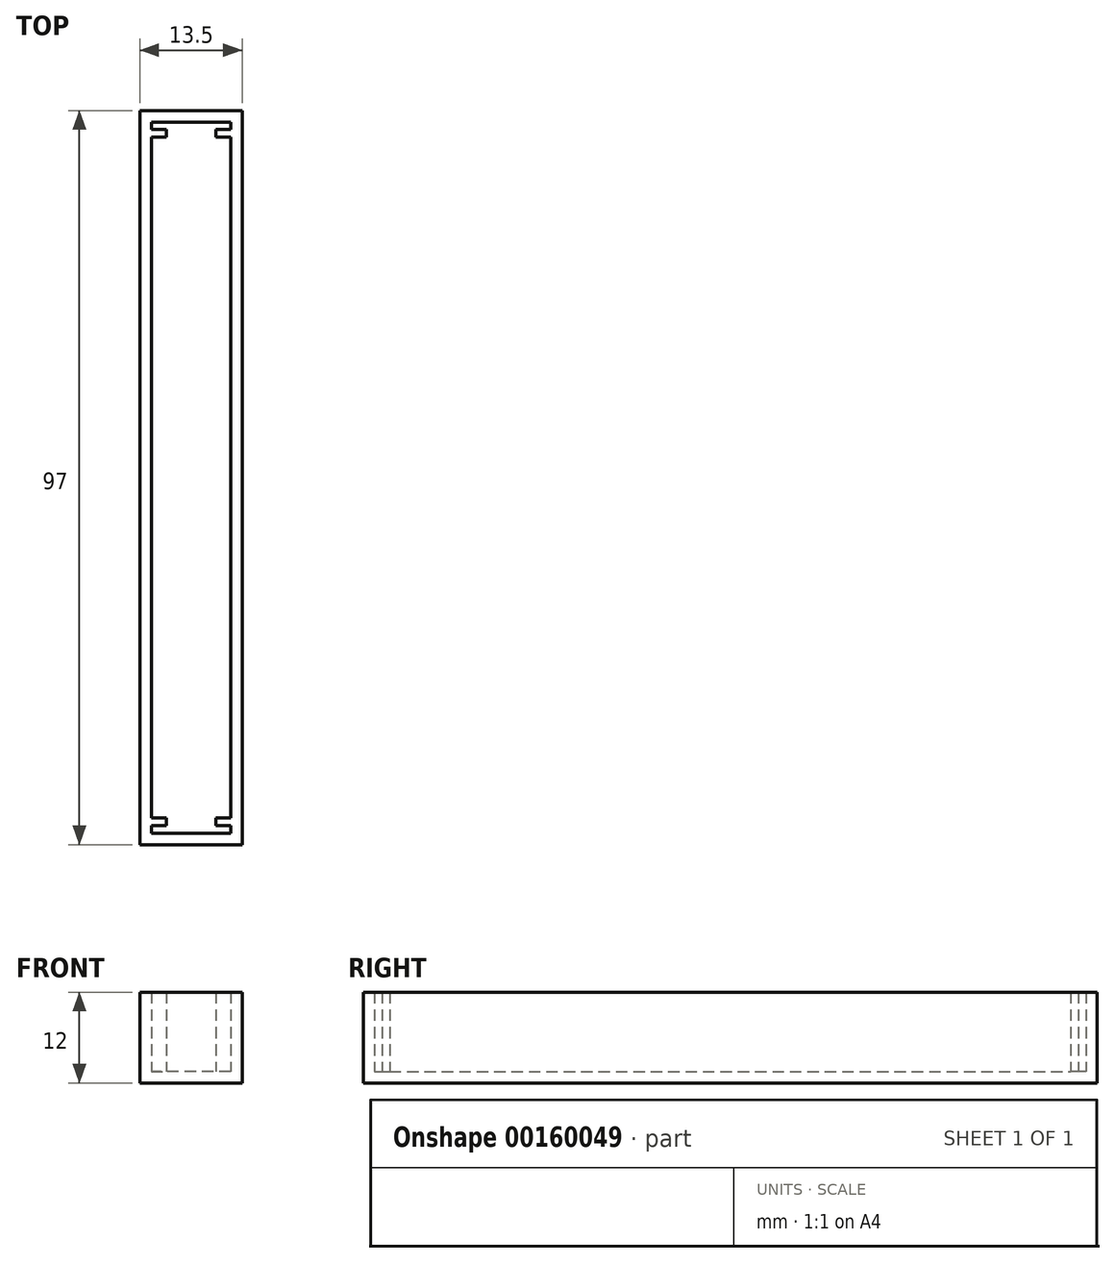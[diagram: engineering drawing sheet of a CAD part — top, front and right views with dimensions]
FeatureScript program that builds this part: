
annotation { "Feature Type Name" : "Feature", "Feature Type Description" : "" }
export const myFeature = defineFeature(function(context is Context, id is Id, definition is map)
    precondition{}
    {
        {
            var Q0;
            Q0=qCreatedBy(makeId("Top.planeOp"),FACE);
            var sketch = newSketch(context, id + "F0", { "sketchPlane" : qUnion([Q0])});
            skLineSegment(sketch, "E0.bottom", {"start": v(5.25, -47) * mm, "end": v(-5.25, -47) * mm});
            skLineSegment(sketch, "E0.top", {"start": v(5.25, 47) * mm, "end": v(-5.25, 47) * mm});
            skLineSegment(sketch, "E0.left", {"start": v(5.25, -47) * mm, "end": v(5.25, -46) * mm});
            skLineSegment(sketch, "E0.right", {"start": v(-5.25, -47) * mm, "end": v(-5.25, -46) * mm});
            skPoint(sketch, "E0.middle", {"position": v(0, 0) * mm});
            skLineSegment(sketch, "E1", {"start": v(5.25, 47) * mm, "end": v(5.25, 46) * mm});
            skLineSegment(sketch, "E2", {"start": v(5.25, 46) * mm, "end": v(3.25, 46) * mm});
            skLineSegment(sketch, "E3", {"start": v(3.25, 46) * mm, "end": v(3.25, 45) * mm});
            skLineSegment(sketch, "E4", {"start": v(3.25, 45) * mm, "end": v(5.25, 45) * mm});
            skLineSegment(sketch, "E5.MirrorCS", {"start": v(-3.25, 45) * mm, "end": v(-5.25, 45) * mm});
            skLineSegment(sketch, "E6.MirrorCS", {"start": v(-3.25, 46) * mm, "end": v(-3.25, 45) * mm});
            skLineSegment(sketch, "E7.MirrorCS", {"start": v(-5.25, 46) * mm, "end": v(-3.25, 46) * mm});
            skLineSegment(sketch, "E8.MirrorCS", {"start": v(-5.25, 47) * mm, "end": v(-5.25, 46) * mm});
            skLineSegment(sketch, "E9.MirrorCS", {"start": v(-5.25, -46) * mm, "end": v(-3.25, -46) * mm});
            skLineSegment(sketch, "E10.MirrorCS", {"start": v(-3.25, -46) * mm, "end": v(-3.25, -45) * mm});
            skLineSegment(sketch, "E11.MirrorCS", {"start": v(-3.25, -45) * mm, "end": v(-5.25, -45) * mm});
            skLineSegment(sketch, "E12.MirrorCS", {"start": v(3.25, -45) * mm, "end": v(5.25, -45) * mm});
            skLineSegment(sketch, "E13.MirrorCS", {"start": v(5.25, -46) * mm, "end": v(3.25, -46) * mm});
            skLineSegment(sketch, "E14.MirrorCS", {"start": v(3.25, -46) * mm, "end": v(3.25, -45) * mm});
            skLineSegment(sketch, "E15.bottom", {"start": v(6.75, -48.5) * mm, "end": v(-6.75, -48.5) * mm});
            skLineSegment(sketch, "E15.top", {"start": v(6.75, 48.5) * mm, "end": v(-6.75, 48.5) * mm});
            skLineSegment(sketch, "E15.left", {"start": v(6.75, -48.5) * mm, "end": v(6.75, 48.5) * mm});
            skLineSegment(sketch, "E15.right", {"start": v(-6.75, -48.5) * mm, "end": v(-6.75, 48.5) * mm});
            skLineSegment(sketch, "E16.trimOffspring", {"start": v(5.25, 46) * mm, "end": v(5.25, 47) * mm});
            skLineSegment(sketch, "E17.trimOffspring", {"start": v(-5.25, 46) * mm, "end": v(-5.25, 47) * mm});
            skLineSegment(sketch, "E18.trimOffspring", {"start": v(5.25, -45) * mm, "end": v(5.25, 45) * mm});
            skLineSegment(sketch, "E19.trimOffspring", {"start": v(-5.25, -45) * mm, "end": v(-5.25, 45) * mm});
            skSolve(sketch);
        }
        {
            var Q0;
            Q0=qCreatedBy(makeId("Top.planeOp"),FACE);
            var sketch = newSketch(context, id + "F1", { "sketchPlane" : qUnion([Q0])});
            skLineSegment(sketch, "E20.bottom", {"start": v(6.75, -48.5) * mm, "end": v(-6.75, -48.5) * mm});
            skLineSegment(sketch, "E20.top", {"start": v(6.75, 48.5) * mm, "end": v(-6.75, 48.5) * mm});
            skLineSegment(sketch, "E20.left", {"start": v(6.75, -48.5) * mm, "end": v(6.75, 48.5) * mm});
            skLineSegment(sketch, "E20.right", {"start": v(-6.75, -48.5) * mm, "end": v(-6.75, 48.5) * mm});
            skPoint(sketch, "E20.middle", {"position": v(0, 0) * mm});
            skSolve(sketch);
        }
        {
            var Q0;
            Q0 = qSketchRegion(id + "F0", true);
            extrude(context, id + "F2", {"entities" : qUnion([Q0]), "depth" : 12 * mm});
        }
        {
            var Q0;
            Q0 = qSketchRegion(id + "F1", true);
            extrude(context, id + "F3", {"entities" : qUnion([Q0]), "operationType" : NewBodyOperationType.ADD, "depth" : 1.5 * mm});
        }
    });
